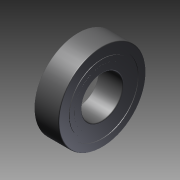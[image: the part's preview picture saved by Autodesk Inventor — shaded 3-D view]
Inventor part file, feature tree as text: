
AUTODESK INVENTOR PART (.ipt)
format: ipt  version: 2016 (Build 200138000, 138)  size: 167,424 bytes
history: native  units: mm
features: other x7, revolve x3, sketch x3
ambient origin geometry x8: Origin, YZ Plane, XZ Plane, XY Plane, X Axis, Y Axis, Z Axis, Center Point
bodies: Solid1 (feature_tree)
feature tree (13):
  revolve  "Revolution1"  Angle=360.0deg
  revolve  "Revolution2"  [1 undecoded]
  revolve  "Revolution3"  [1 undecoded]
  other  "bf_2_XY"
  other  "bf_2_YZ"
  other  "bf_2_ZX"
  other  "bf_2_X"
  other  "bf_2_Y"
  other  "bf_2_Z"
  other  "bf_2_Center"
  sketch  "Sketch_1"  dims[d0=360.0deg d1=360.0deg]
  sketch  "Sketch_2"  dims[d2=360.0deg]
  sketch  "Sketch_3"
note: 2 required parameter values undecoded (feature->parameter linkage not recoverable at this tier; creation-order binding heuristic only, values carry confidence <= 0.55)
